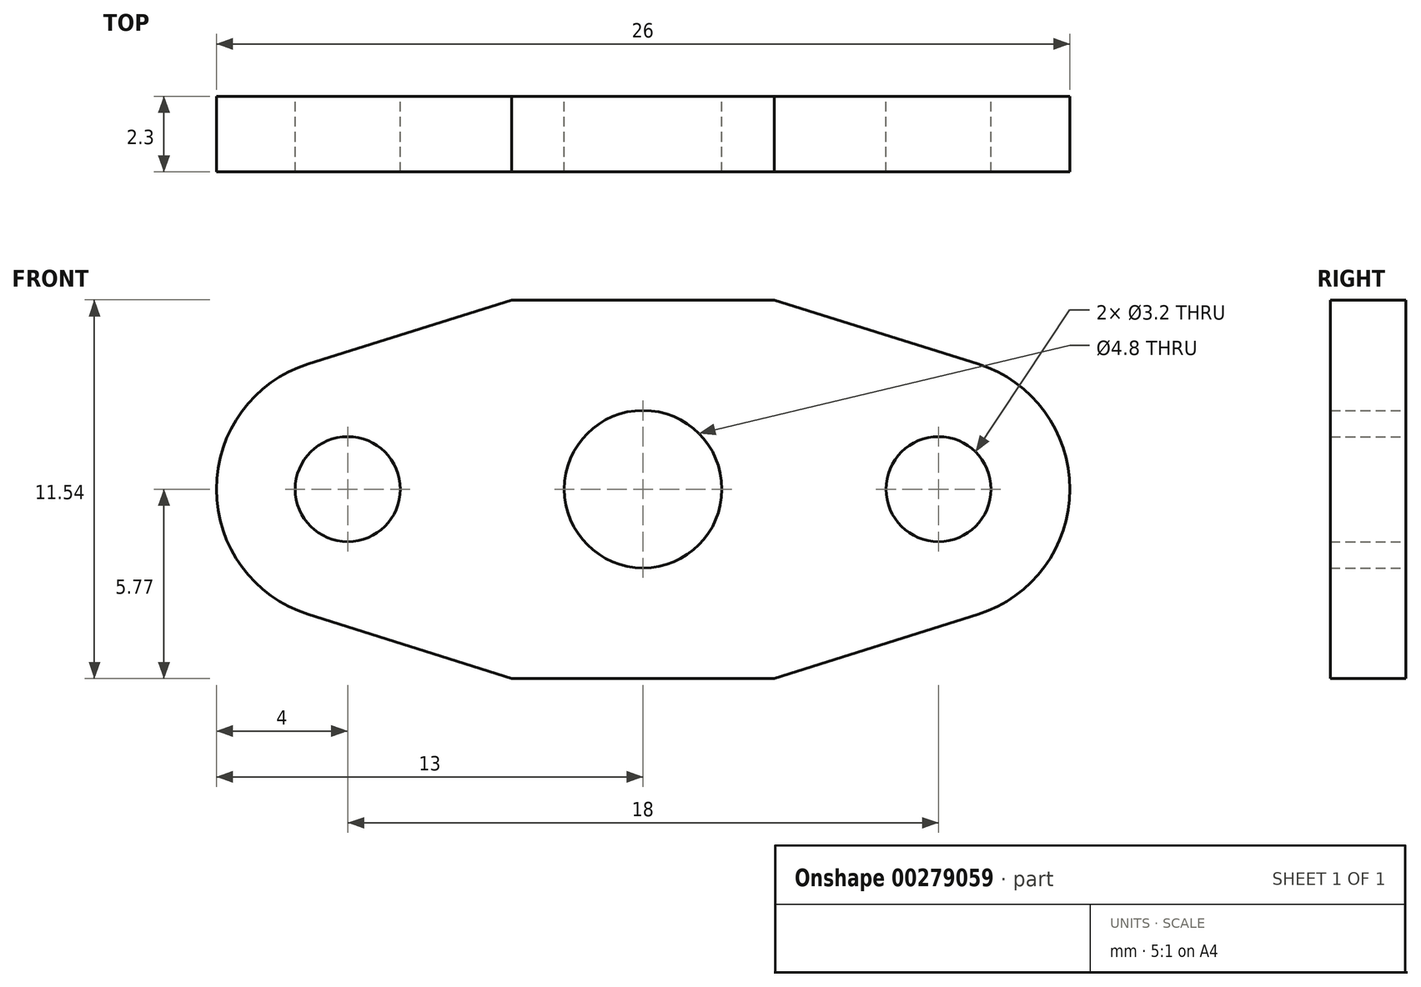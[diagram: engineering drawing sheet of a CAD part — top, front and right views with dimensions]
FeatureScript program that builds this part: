
annotation { "Feature Type Name" : "Feature", "Feature Type Description" : "" }
export const myFeature = defineFeature(function(context is Context, id is Id, definition is map)
    precondition{}
    {
        {
            var Q0;
            Q0=qCreatedBy(makeId("Front.planeOp"),FACE);
            var sketch = newSketch(context, id + "F0", { "sketchPlane" : qUnion([Q0])});
            skLineSegment(sketch, "E0.bottom", {"start": v(-13, 36.3) * mm, "end": v(13, 36.3) * mm});
            skLineSegment(sketch, "E0.top", {"start": v(-13, 34) * mm, "end": v(13, 34) * mm});
            skLineSegment(sketch, "E0.left", {"start": v(-13, 36.3) * mm, "end": v(-13, 34) * mm});
            skLineSegment(sketch, "E0.right", {"start": v(13, 36.3) * mm, "end": v(13, 34) * mm});
            skPoint(sketch, "E0.middle", {"position": v(0, 35.15) * mm});
            skLineSegment(sketch, "E1.bottom", {"start": v(-6.5, 26.3) * mm, "end": v(6.5, 26.3) * mm});
            skLineSegment(sketch, "E1.top", {"start": v(-6.5, 5) * mm, "end": v(6.5, 5) * mm});
            skLineSegment(sketch, "E1.left", {"start": v(-6.5, 26.3) * mm, "end": v(-6.5, 5) * mm});
            skLineSegment(sketch, "E1.right", {"start": v(6.5, 26.3) * mm, "end": v(6.5, 5) * mm});
            skPoint(sketch, "E1.middle", {"position": v(0, 15.65) * mm});
            skLineSegment(sketch, "E2.bottom", {"start": v(-5.5, 34) * mm, "end": v(5.5, 34) * mm});
            skLineSegment(sketch, "E2.top", {"start": v(-5.5, 26.3) * mm, "end": v(5.5, 26.3) * mm});
            skLineSegment(sketch, "E2.left", {"start": v(-5.5, 34) * mm, "end": v(-5.5, 26.3) * mm});
            skLineSegment(sketch, "E2.right", {"start": v(5.5, 34) * mm, "end": v(5.5, 26.3) * mm});
            skPoint(sketch, "E2.middle", {"position": v(0, 30.15) * mm});
            skLineSegment(sketch, "E3", {"start": v(-6.5, 5) * mm, "end": v(-6.5, 3) * mm});
            skLineSegment(sketch, "E4", {"start": v(-6.5, 3) * mm, "end": v(-3.5, 0) * mm});
            skLineSegment(sketch, "E5", {"start": v(-3.5, 0) * mm, "end": v(0, 0) * mm});
            skLineSegment(sketch, "E6.MirrorCS", {"start": v(6.5, 5) * mm, "end": v(6.5, 3) * mm});
            skLineSegment(sketch, "E7.MirrorCS", {"start": v(6.5, 3) * mm, "end": v(3.5, 0) * mm});
            skLineSegment(sketch, "E8.MirrorCS", {"start": v(3.5, 0) * mm, "end": v(0, 0) * mm});
            skLineSegment(sketch, "E9", {"start": v(-1, 0) * mm, "end": v(-1, -5.77) * mm});
            skLineSegment(sketch, "E10", {"start": v(-1, -5.77) * mm, "end": v(0, -5.77) * mm, "construction": true});
            skLineSegment(sketch, "E11.MirrorCS", {"start": v(1, -5.77) * mm, "end": v(0, -5.77) * mm, "construction": true});
            skLineSegment(sketch, "E12.MirrorCS", {"start": v(1, 0) * mm, "end": v(1, -5.77) * mm});
            skLineSegment(sketch, "E13", {"start": v(-6.5, 25.3) * mm, "end": v(6.5, 25.3) * mm});
            skCircle(sketch, "E14", {"center": v(0, -20) * mm, "radius": 2.4 * mm});
            skCircle(sketch, "E15", {"center": v(9, -20) * mm, "radius": 1.6 * mm});
            skArc(sketch, "E16", {"start": v(10.2, -16.18) * mm, "mid": v(13, -20) * mm, "end": v(10.2, -23.82) * mm});
            skLineSegment(sketch, "E17", {"start": v(10.2, -16.18) * mm, "end": v(4, -14.24) * mm});
            skLineSegment(sketch, "E18", {"start": v(4, -14.24) * mm, "end": v(0, -14.24) * mm});
            skLineSegment(sketch, "E19", {"start": v(-4, -25.76) * mm, "end": v(4, -25.76) * mm});
            skLineSegment(sketch, "E20", {"start": v(4, -25.76) * mm, "end": v(10.2, -23.82) * mm});
            skLineSegment(sketch, "E21.MirrorCS", {"start": v(-4, -25.76) * mm, "end": v(-10.2, -23.82) * mm});
            skArc(sketch, "E22.MirrorCS", {"start": v(-10.2, -16.18) * mm, "mid": v(-13, -20) * mm, "end": v(-10.2, -23.82) * mm});
            skLineSegment(sketch, "E23.MirrorCS", {"start": v(-10.2, -16.18) * mm, "end": v(-4, -14.23) * mm});
            skCircle(sketch, "E24.MirrorC", {"center": v(-9, -20) * mm, "radius": 1.6 * mm});
            skLineSegment(sketch, "E25.MirrorCS", {"start": v(-4, -14.23) * mm, "end": v(0, -14.24) * mm});
            skArc(sketch, "E26", {"start": v(1, -5.77) * mm, "mid": v(0, -6.02) * mm, "end": v(-1, -5.77) * mm});
            skSolve(sketch);
        }
        {
            var Q0;
            Q0=makeQuery(id+"F0.imprint","IMPRINT",FACE,{"disambiguationData":[TD([[makeQuery(id+"F0.imprint","IMPRINT",EDGE,{"derivedFrom":sQuery(id+"F0.wireOp",EDGE,"E14")}),-1.0]])]});
            extrude(context, id + "F1", {"entities" : qUnion([Q0]), "depth" : 2.3 * mm});
        }
    });
